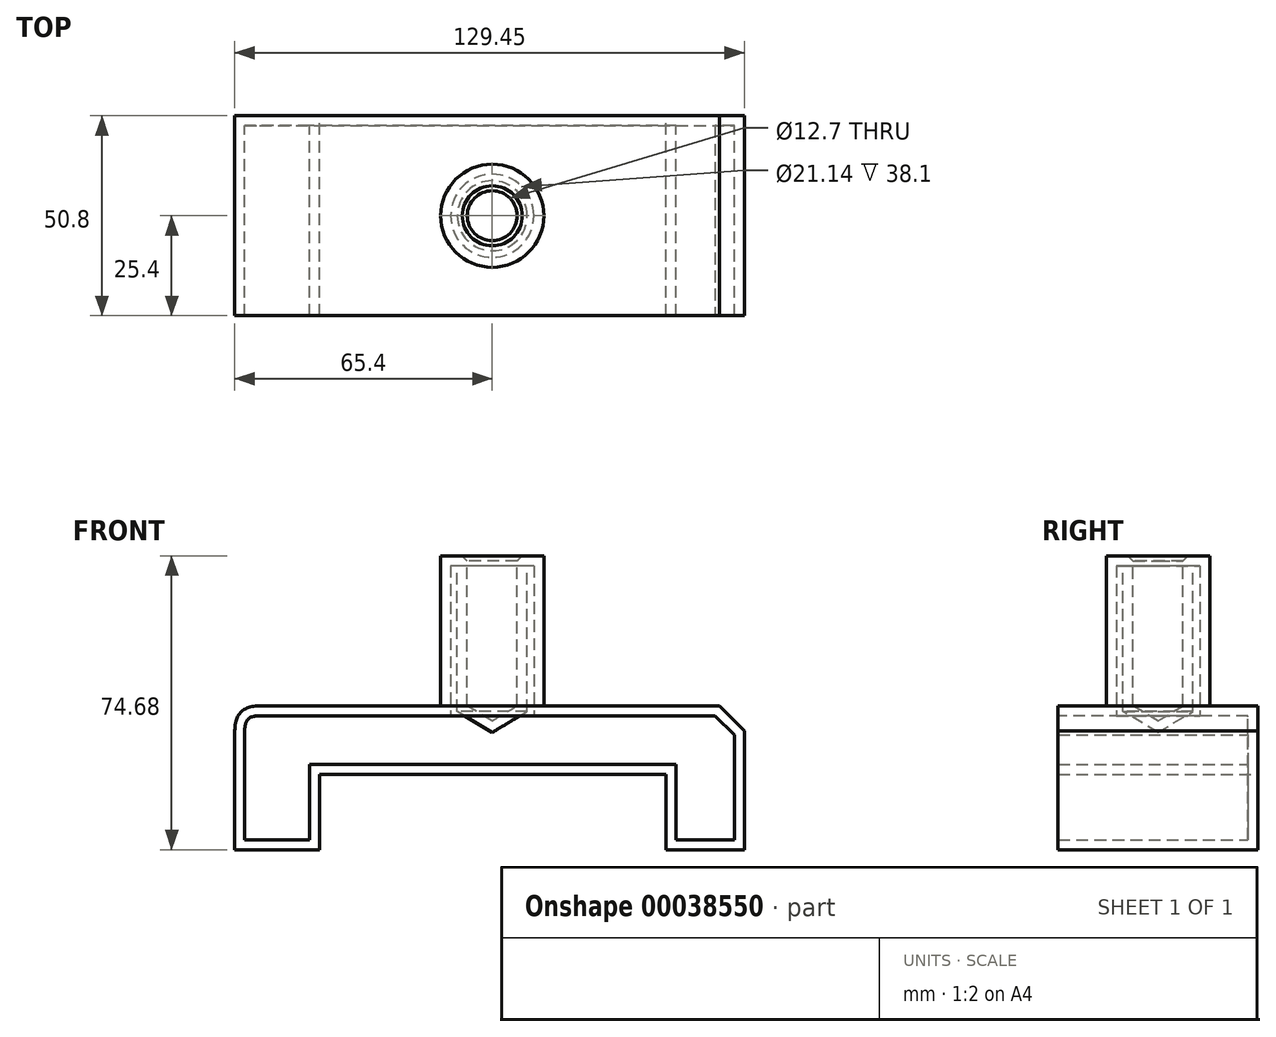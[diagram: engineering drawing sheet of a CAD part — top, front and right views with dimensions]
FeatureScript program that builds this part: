
annotation { "Feature Type Name" : "Feature", "Feature Type Description" : "" }
export const myFeature = defineFeature(function(context is Context, id is Id, definition is map)
    precondition{}
    {
        {
            var Q0;
            Q0=qCreatedBy(makeId("Front.planeOp"),FACE);
            var sketch = newSketch(context, id + "F0", { "sketchPlane" : qUnion([Q0])});
            skLineSegment(sketch, "E0", {"start": v(-65.4, 0) * mm, "end": v(-65.4, 36.58) * mm});
            skLineSegment(sketch, "E1", {"start": v(-65.4, 36.58) * mm, "end": v(64.05, 36.58) * mm});
            skLineSegment(sketch, "E2", {"start": v(64.05, 36.58) * mm, "end": v(64.05, 0) * mm});
            skLineSegment(sketch, "E3", {"start": v(44.16, 0) * mm, "end": v(64.05, 0) * mm});
            skLineSegment(sketch, "E4", {"start": v(44.16, 0) * mm, "end": v(44.16, 19.18) * mm});
            skLineSegment(sketch, "E5", {"start": v(44.16, 19.18) * mm, "end": v(-43.83, 19.18) * mm});
            skLineSegment(sketch, "E6", {"start": v(-43.83, 19.18) * mm, "end": v(-43.83, 0) * mm});
            skLineSegment(sketch, "E7", {"start": v(-43.83, 0) * mm, "end": v(-65.4, 0) * mm});
            skSolve(sketch);
        }
        {
            var Q0;
            Q0=makeQuery(id+"F0.imprint","IMPRINT",FACE,{"disambiguationData":[TD([[makeQuery(id+"F0.imprint","IMPRINT",EDGE,{"derivedFrom":sQuery(id+"F0.wireOp",EDGE,"E0")}),-1.0]])]});
            extrude(context, id + "F1", {"entities" : qUnion([Q0]), "depth" : 50.8 * mm});
        }
        {
            var Q0;
            Q0=makeQuery(id+"F1.opExtrude","SWEPT_EDGE",EDGE,{"disambiguationData":[OSD([sQuery(id+"F0.wireOp",EDGE,"E0"),sQuery(id+"F0.wireOp",EDGE,"E1")])]});
            fillet(context, id + "F2", {"entities" : qUnion([Q0]), "radius" : 6.35 * mm, "tangentPropagation" : true, "rho" : 0.5, "crossSection" : FilletCrossSection.CONIC, "allowEdgeOverflow" : false});
        }
        {
            var Q0;
            Q0=makeQuery(id+"F1.opExtrude","SWEPT_EDGE",EDGE,{"disambiguationData":[OSD([sQuery(id+"F0.wireOp",EDGE,"E1"),sQuery(id+"F0.wireOp",EDGE,"E2")])]});
            chamfer(context, id + "F3", {"entities" : qUnion([Q0]), "width" : 6.35 * mm, "tangentPropagation" : true});
        }
        {
            var Q0;
            Q0=makeQuery(id+"F1.opExtrude","SWEPT_FACE",FACE,{"disambiguationData":[OSD([sQuery(id+"F0.wireOp",EDGE,"E1")])]});
            var sketch = newSketch(context, id + "F4", { "sketchPlane" : qUnion([Q0])});
            skCircle(sketch, "E8", {"center": v(0, -25.4) * mm, "radius": 13.11 * mm});
            skPoint(sketch, "E8.centerSnap0", {"position": v(57.7, -25.4) * mm});
            skSolve(sketch);
        }
        {
            var Q0;
            Q0=makeQuery(id+"F4.imprint","IMPRINT",FACE,{"disambiguationData":[TD([[makeQuery(id+"F4.imprint","IMPRINT",EDGE,{"derivedFrom":sQuery(id+"F4.wireOp",EDGE,"E8")}),1.0]])]});
            extrude(context, id + "F5", {"entities" : qUnion([Q0]), "operationType" : NewBodyOperationType.ADD, "depth" : 38.1 * mm});
        }
        {
            var Q0;
            Q0=makeQuery(id+"F5.opExtrude","CAP_FACE",FACE,{"disambiguationData":[OSD([sQuery(id+"F4.wireOp",EDGE,"E8")])],"isStart":false});
            var sketch = newSketch(context, id + "F6", { "sketchPlane" : qUnion([Q0])});
            skPoint(sketch, "E9", {"position": v(0, -25.4) * mm});
            skSolve(sketch);
        }
        {
            var Q0;
            Q0=sQuery(id+"F6.wireOp",VERTEX,"E9");
            var Q1;
            Q1=makeQuery(id+"F1.opExtrude","SWEPT_BODY",BODY,{"disambiguationData":[OSD([sQuery(id+"F0.wireOp",EDGE,"E0"),sQuery(id+"F0.wireOp",EDGE,"E1"),sQuery(id+"F0.wireOp",EDGE,"E2"),sQuery(id+"F0.wireOp",EDGE,"E3"),sQuery(id+"F0.wireOp",EDGE,"E4"),sQuery(id+"F0.wireOp",EDGE,"E5"),sQuery(id+"F0.wireOp",EDGE,"E6"),sQuery(id+"F0.wireOp",EDGE,"E7")])]});
            hole(context, id + "F7", {"style" : HoleStyle.C_SINK, "holeDiameter" : 12.7 * mm, "cSinkDiameter" : 15.24 * mm, "endStyle" : HoleEndStyle.BLIND, "holeDepth" : 38.1 * mm, "locations" : qUnion([Q0]), "scope" : qUnion([Q1]), "cSinkAngle" : 90 * degree});
        }
        {
            var Q0;
            Q0=makeQuery(id+"F1.opExtrude","CAP_FACE",FACE,{"disambiguationData":[OSD([sQuery(id+"F0.wireOp",EDGE,"E0"),sQuery(id+"F0.wireOp",EDGE,"E1"),sQuery(id+"F0.wireOp",EDGE,"E2"),sQuery(id+"F0.wireOp",EDGE,"E3"),sQuery(id+"F0.wireOp",EDGE,"E4"),sQuery(id+"F0.wireOp",EDGE,"E5"),sQuery(id+"F0.wireOp",EDGE,"E6"),sQuery(id+"F0.wireOp",EDGE,"E7")])],"isStart":false});
            shell(context, id + "F8", {"entities" : qUnion([Q0]), "thickness" : 2.54 * mm});
        }
    });
